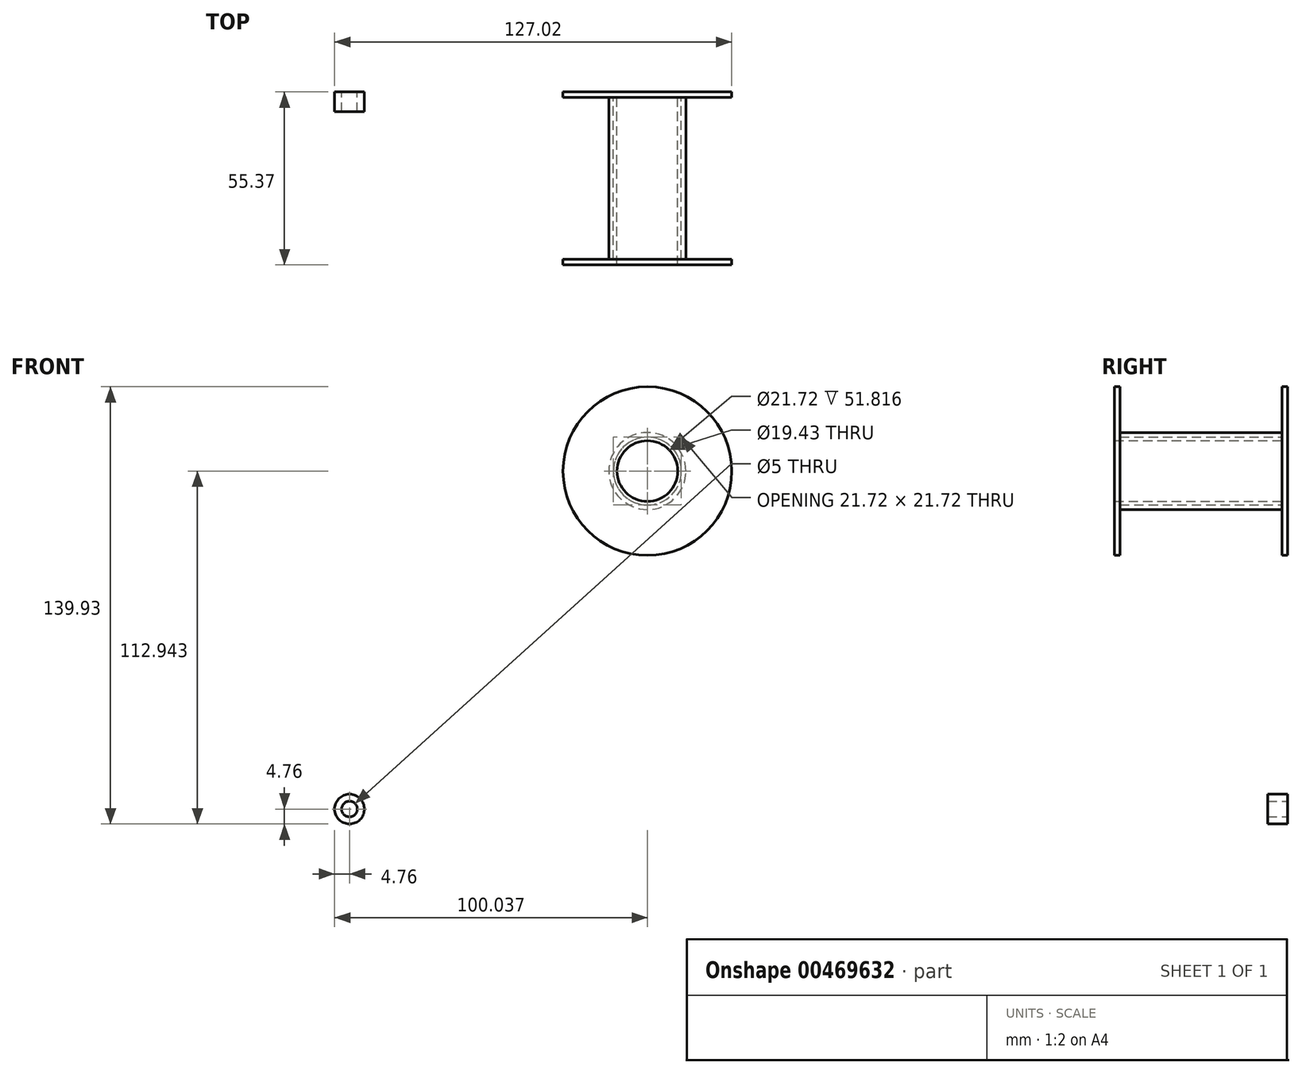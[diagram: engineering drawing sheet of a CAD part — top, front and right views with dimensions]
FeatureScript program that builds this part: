
annotation { "Feature Type Name" : "Feature", "Feature Type Description" : "" }
export const myFeature = defineFeature(function(context is Context, id is Id, definition is map)
    precondition{}
    {
        {
            var Q0;
            Q0=qCreatedBy(makeId("Front.planeOp"),FACE);
            var sketch = newSketch(context, id + "F0", { "sketchPlane" : qUnion([Q0])});
            skCircle(sketch, "E0", {"center": v(0, 0) * mm, "radius": 2.5 * mm});
            skCircle(sketch, "E1", {"center": v(0, 0) * mm, "radius": 4.76 * mm});
            skSolve(sketch);
        }
        {
            var Q0;
            Q0=makeQuery(id+"F0.imprint","IMPRINT",FACE,{"disambiguationData":[TD([[makeQuery(id+"F0.imprint","IMPRINT",EDGE,{"derivedFrom":sQuery(id+"F0.wireOp",EDGE,"E0")}),-1.0]])]});
            extrude(context, id + "F1", {"entities" : qUnion([Q0]), "depth" : 6.35 * mm});
        }
        {
            var Q0;
            Q0=qCreatedBy(makeId("Front.planeOp"),FACE);
            var sketch = newSketch(context, id + "F2", { "sketchPlane" : qUnion([Q0])});
            skCircle(sketch, "E2", {"center": v(95.28, 108.18) * mm, "radius": 10.86 * mm});
            skCircle(sketch, "E3", {"center": v(95.28, 108.18) * mm, "radius": 9.72 * mm});
            skSolve(sketch);
        }
        {
            var Q0;
            Q0 = qSketchRegion(id + "F2", true);
            extrude(context, id + "F3", {"entities" : qUnion([Q0]), "depth" : 55.37 * mm, "offsetDistance" : 25.4 * mm});
        }
        {
            var Q0;
            Q0=makeQuery(id+"F3.opExtrude","CAP_FACE",FACE,{"disambiguationData":[OSD([sQuery(id+"F2.wireOp",EDGE,"E2"),sQuery(id+"F2.wireOp",EDGE,"E3")])],"isStart":false});
            var sketch = newSketch(context, id + "F4", { "sketchPlane" : qUnion([Q0])});
            skCircle(sketch, "E4", {"center": v(95.28, 108.18) * mm, "radius": 26.99 * mm});
            skCircle(sketch, "E5", {"center": v(95.28, 108.18) * mm, "radius": 9.72 * mm});
            skSolve(sketch);
        }
        {
            var Q0;
            Q0 = qSketchRegion(id + "F4", true);
            extrude(context, id + "F5", {"entities" : qUnion([Q0]), "operationType" : NewBodyOperationType.ADD, "oppositeDirection" : true, "depth" : 1.78 * mm, "offsetDistance" : 25.4 * mm});
        }
        {
            var Q0;
            Q0=makeQuery(id+"F3.opExtrude","CAP_FACE",FACE,{"disambiguationData":[OSD([sQuery(id+"F2.wireOp",EDGE,"E2"),sQuery(id+"F2.wireOp",EDGE,"E3")])],"isStart":true});
            var sketch = newSketch(context, id + "F6", { "sketchPlane" : qUnion([Q0])});
            skCircle(sketch, "E6", {"center": v(-95.28, 108.18) * mm, "radius": 26.99 * mm});
            skCircle(sketch, "E7", {"center": v(-95.28, 108.18) * mm, "radius": 9.72 * mm});
            skSolve(sketch);
        }
        {
            var Q0;
            Q0 = qSketchRegion(id + "F6", true);
            extrude(context, id + "F7", {"entities" : qUnion([Q0]), "operationType" : NewBodyOperationType.ADD, "oppositeDirection" : true, "depth" : 1.78 * mm, "offsetDistance" : 25.4 * mm});
        }
        {
            var Q0;
            Q0=makeQuery(id+"F7.opExtrude","CAP_FACE",FACE,{"disambiguationData":[OSD([sQuery(id+"F6.wireOp",EDGE,"E6"),sQuery(id+"F6.wireOp",EDGE,"E7")])],"isStart":false});
            var sketch = newSketch(context, id + "F8", { "sketchPlane" : qUnion([Q0])});
            skCircle(sketch, "E8", {"center": v(95.28, 108.18) * mm, "radius": 10.86 * mm});
            skCircle(sketch, "E9", {"center": v(95.28, 108.18) * mm, "radius": 12.33 * mm});
            skSolve(sketch);
        }
        {
            var Q0;
            Q0 = qSketchRegion(id + "F8", true);
            var Q1;
            Q1=makeQuery(id+"F5.opExtrude","CAP_FACE",FACE,{"disambiguationData":[OSD([sQuery(id+"F4.wireOp",EDGE,"E4"),sQuery(id+"F4.wireOp",EDGE,"E5")])],"isStart":false});
            extrude(context, id + "F9", {"entities" : qUnion([Q0]), "endBound" : BoundingType.UP_TO_SURFACE, "depth" : 25.4 * mm, "endBoundEntityFace" : qUnion([Q1]), "offsetDistance" : 25.4 * mm});
        }
    });
